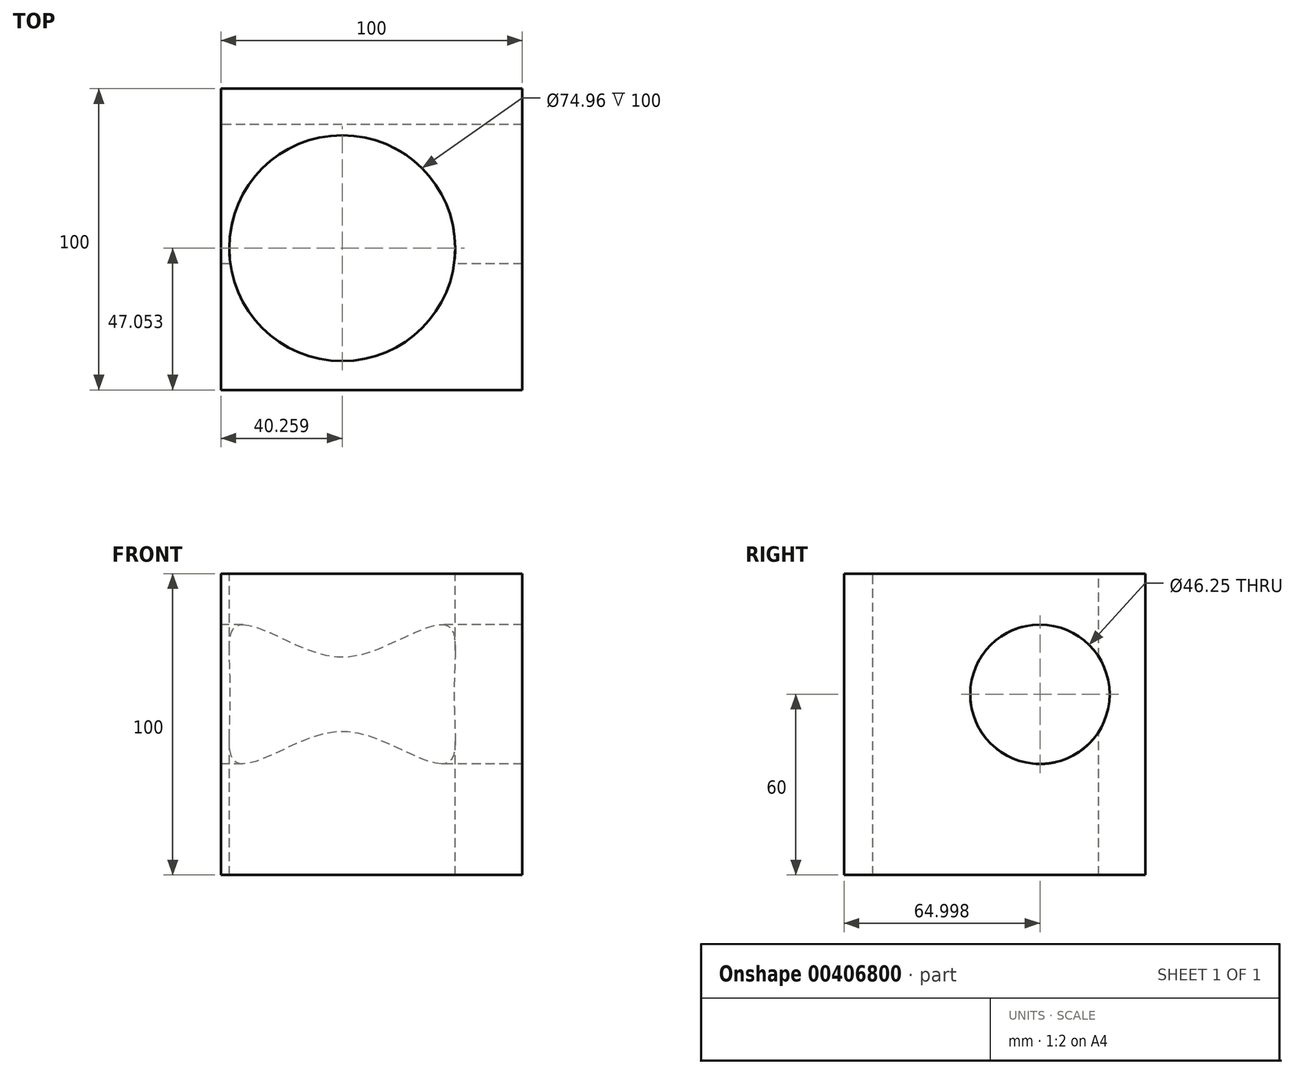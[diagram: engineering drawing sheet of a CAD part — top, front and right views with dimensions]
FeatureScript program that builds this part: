
annotation { "Feature Type Name" : "Feature", "Feature Type Description" : "" }
export const myFeature = defineFeature(function(context is Context, id is Id, definition is map)
    precondition{}
    {
        {
            var Q0;
            Q0=qCreatedBy(makeId("Top.planeOp"),FACE);
            var sketch = newSketch(context, id + "F0", { "sketchPlane" : qUnion([Q0])});
            skLineSegment(sketch, "E0.bottom", {"start": v(-51.54, 59.26) * mm, "end": v(48.46, 59.26) * mm});
            skLineSegment(sketch, "E0.top", {"start": v(-51.54, -40.74) * mm, "end": v(48.46, -40.74) * mm});
            skLineSegment(sketch, "E0.left", {"start": v(-51.54, 59.26) * mm, "end": v(-51.54, -40.74) * mm});
            skLineSegment(sketch, "E0.right", {"start": v(48.46, 59.26) * mm, "end": v(48.46, -40.74) * mm});
            skSolve(sketch);
        }
        {
            var Q0;
            Q0 = qSketchRegion(id + "F0", true);
            extrude(context, id + "F1", {"entities" : qUnion([Q0]), "depth" : 100 * mm});
        }
        {
            var Q0;
            Q0=makeQuery(id+"F1.opExtrude","CAP_FACE",FACE,{"disambiguationData":[OSD([sQuery(id+"F0.wireOp",EDGE,"E0.bottom"),sQuery(id+"F0.wireOp",EDGE,"E0.top"),sQuery(id+"F0.wireOp",EDGE,"E0.left"),sQuery(id+"F0.wireOp",EDGE,"E0.right")])],"isStart":false});
            var sketch = newSketch(context, id + "F2", { "sketchPlane" : qUnion([Q0])});
            skCircle(sketch, "E1", {"center": v(-11.28, 6.31) * mm, "radius": 37.48 * mm});
            skCircle(sketch, "E2.0", {"center": v(-11.28, 6.31) * mm, "radius": 39.48 * mm});
            skSolve(sketch);
        }
        {
            var Q0;
            Q0=makeQuery(id+"F2.imprint","IMPRINT",FACE,{"disambiguationData":[TD([[makeQuery(id+"F2.imprint","IMPRINT",EDGE,{"derivedFrom":sQuery(id+"F2.wireOp",EDGE,"E1")}),1.0]])]});
            var Q1;
            Q1 = qBodyType(qCreatedBy(id + "F2" ,EDGE), BodyType.WIRE);
            var Q2;
            Q2=sQuery(id+"F2.wireOp",EDGE,"E1");
            extrude(context, id + "F3", {"entities" : qUnion([Q0]), "operationType" : NewBodyOperationType.REMOVE, "surfaceEntities" : qUnion([Q1, Q2]), "endBound" : BoundingType.THROUGH_ALL, "oppositeDirection" : true, "depth" : 25 * mm});
        }
        {
            var Q0;
            Q0=makeQuery(id+"F1.opExtrude","SWEPT_FACE",FACE,{"disambiguationData":[OSD([sQuery(id+"F0.wireOp",EDGE,"E0.left")])]});
            var sketch = newSketch(context, id + "F4", { "sketchPlane" : qUnion([Q0])});
            skCircle(sketch, "E3", {"center": v(-24.26, 60) * mm, "radius": 23.13 * mm});
            skSolve(sketch);
        }
        {
            var Q0;
            Q0 = qSketchRegion(id + "F4", true);
            extrude(context, id + "F5", {"entities" : qUnion([Q0]), "operationType" : NewBodyOperationType.REMOVE, "endBound" : BoundingType.THROUGH_ALL, "oppositeDirection" : true, "depth" : 25 * mm});
        }
    });
